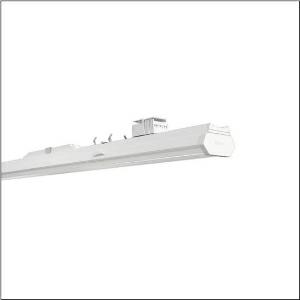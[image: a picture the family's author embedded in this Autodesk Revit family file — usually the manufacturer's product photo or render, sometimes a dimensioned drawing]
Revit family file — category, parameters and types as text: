
# Revit family: licross_11_protected_ho_51tp12dn4fxmd
name_source: partatom
category: Lighting Fixtures
units: mm (PartAtom-declared; Revit-internal decimal feet)

## family parameters
Cut with Voids When Loaded = No
Host = Face
Light Source = No
Part Type = Normal
Room Calculation Point = No
Round Connector Dimension = Use Diameter
Shared = No

## types (1)
- --- (1 x LED, 2290 lm, 13.9 W, 4000K)
    Apparent Load = 14 VA
    CIE Flux Codes = 70 91 97 98 100
    Color Rendering = 80
    Color Temperature = 4000K
    Default Elevation = 1800 mm
    Description = Licross 11 Protected HO, luminaire insert, of sheet steel, galvanised, coil coated, white, length: 1.500mm, width: 90mm, height: 101mm, LED rated luminous flux: 15.270lm, light colour: 840, SDCM (Standard Deviation of Colour Matching)MacAdam ≤ 2 SDCM (initial), control gear: DALI 2 (for two DALI lines), with plug, 6-pole, with phase selection, mains connection: 220..240V, AC/DC, 0/50..60Hz, rated input power: 87W, internal wiring halogen-free, for central battery installations according to EN 60598-2-22, for emergency light function, without changeover relay, primary optical cover: cover, of PMMA, light emission: direct distribution, primary light characteristic: symmetric, protection rating (complete): IP64, insulation class (complete): insulation class I (protective earthing), certification: CE, ENEC, VDE, UKCA, protection symbol: D if used in an environment with conductive dust loads with corresponding accessories, impact resistance: IK06, permissible ambient temperature for indoor applications: -25..+30°C, standard: EN 60598-2-22, corresponds to IFS (International Featured Standards) requirements for safety and quality in the food industry, reducing of maximum allowable ambient temperature of 5°C with ceiling mounting, LABS conformity tested according to VDMA 24364:2018-05, The light source and the operating device comply with the requirements of the Ecodesign Regulation (EU) 2019/2020 and are replaceable in accordance with this regulation, packaging unit: 1 piece
    Height = 92 mm
    Lamp = 1 x LED
    Lamp Light Flux = 2290 lm
    Lamp Power = 13.9 W
    Lamp count = 1
    Length = 1500 mm
    Luminous efficacy = 165 lm/W
    Manufacturer = Siteco
    ModVariant = No
    Model = 51TP12DN4FXMD
    Mounting Place = Ceiling
    Mounting Type = Pendant
    Number of Poles = 1
    OnlyDefault = Yes
    Power Factor = 1
    Product Name = Licross 11 Protected HO
    Product group = luminaire insert | ceiling pendant
    ProductGroupID = 901
    Protection Class = Protection class I
    Protection Degree = IP 64
    RLX_Detail_Level = 1
    RLX_Emergency_Light_Flux = 0 lm
    RLX_Emergency_Type = 0
    RLX_Emergency_Type_DB = No
    RlxData = <blob elided: 25113 chars, md5=c637ae7e>
    Socket = socket
    Standby Power = 0 W
    System Light Flux = 2290 lm
    System Power = 14 W
    Type Comments = : DC mode (central or group accumulator) initial emergency light level
    Type Image = l_1256148.jpg
    URL = http://relux.com
    VarID = @adj_091617
    Voltage = 0 V
    Weight = 0.00 kg
    Width = 88 mm

## geometry (parser evidence)
native form markers: Blend x4, Sweep x11
no freeform markers — native parametric forms only
